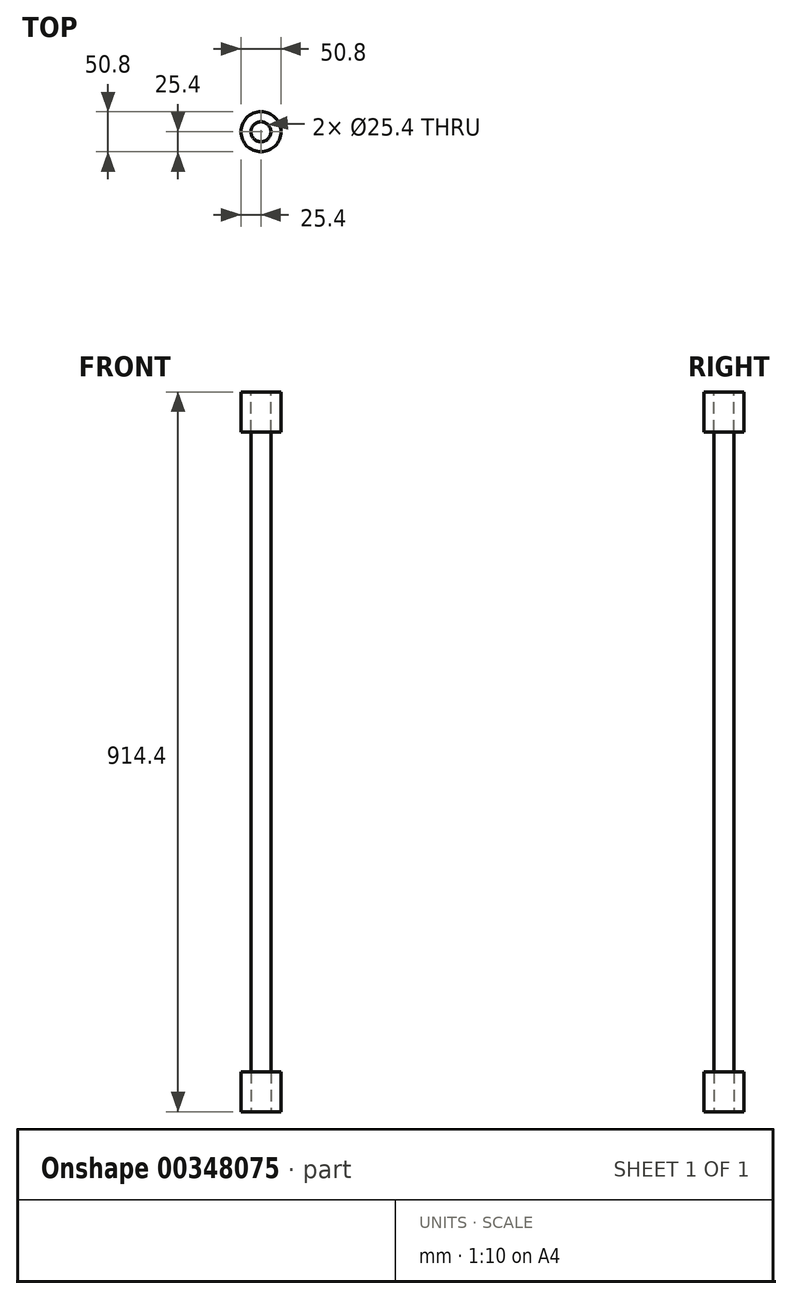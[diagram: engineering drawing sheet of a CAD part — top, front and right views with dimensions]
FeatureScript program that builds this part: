
annotation { "Feature Type Name" : "Feature", "Feature Type Description" : "" }
export const myFeature = defineFeature(function(context is Context, id is Id, definition is map)
    precondition{}
    {
        {
            var Q0;
            Q0=qCreatedBy(makeId("Top.planeOp"),FACE);
            var sketch = newSketch(context, id + "F0", { "sketchPlane" : qUnion([Q0])});
            skCircle(sketch, "E0", {"center": v(0, 0) * mm, "radius": 12.7 * mm});
            skSolve(sketch);
        }
        {
            var Q0;
            Q0=makeQuery(id+"F0.imprint","IMPRINT",FACE,{"disambiguationData":[TD([[makeQuery(id+"F0.imprint","IMPRINT",EDGE,{"derivedFrom":sQuery(id+"F0.wireOp",EDGE,"E0")}),1.0]])]});
            extrude(context, id + "F1", {"entities" : qUnion([Q0]), "depth" : 914.4 * mm});
        }
        {
            var Q0;
            Q0=makeQuery(id+"F1.opExtrude","CAP_FACE",FACE,{"disambiguationData":[OSD([sQuery(id+"F0.wireOp",EDGE,"E0")])],"isStart":false});
            var sketch = newSketch(context, id + "F2", { "sketchPlane" : qUnion([Q0])});
            skCircle(sketch, "E1", {"center": v(0, 0) * mm, "radius": 25.4 * mm});
            skSolve(sketch);
        }
        {
            var Q0;
            Q0=makeQuery(id+"F2.imprint","IMPRINT",FACE,{"disambiguationData":[TD([[makeQuery(id+"F2.imprint","IMPRINT",EDGE,{"derivedFrom":sQuery(id+"F2.wireOp",EDGE,"E1")}),1.0]])]});
            extrude(context, id + "F3", {"entities" : qUnion([Q0]), "oppositeDirection" : true, "depth" : 50.8 * mm});
        }
        {
            var Q0;
            Q0=makeQuery(id+"F1.opExtrude","CAP_FACE",FACE,{"disambiguationData":[OSD([sQuery(id+"F0.wireOp",EDGE,"E0")])],"isStart":true});
            var sketch = newSketch(context, id + "F4", { "sketchPlane" : qUnion([Q0])});
            skCircle(sketch, "E2", {"center": v(0, 0) * mm, "radius": 25.4 * mm});
            skSolve(sketch);
        }
        {
            var Q0;
            Q0=makeQuery(id+"F4.imprint","IMPRINT",FACE,{"disambiguationData":[TD([[makeQuery(id+"F4.imprint","IMPRINT",EDGE,{"derivedFrom":sQuery(id+"F4.wireOp",EDGE,"E2")}),1.0]])]});
            extrude(context, id + "F5", {"entities" : qUnion([Q0]), "oppositeDirection" : true, "depth" : 50.8 * mm});
        }
    });
